# Revit family: BE_99408_de_DE
name_source: partatom
category: Leuchten
revit_build: Autodesk Revit 2015 (Build: 20160512_0715(x64)
units: mm (PartAtom-declared; Revit-internal decimal feet)

## types (4) — shared parameters
AC/DC = AC/DC
Aktualisierung = 2016-10-11T04:14:01
Anschlussleitung = 6.0 m X05BQ-F 4 × 1²
BEGA_Dummy = Nein
BEGA_IES = Ja
BEGA_Intern = Ja
BEGA_Intern_Konstruktion = Ja
BEGA_Intern_an = Ja
BEGA_Intern_aus = Ja
Beschreibung = Aufsatzleuchte
Beschreibung_Sonderanfertigung = Hier können Sie Informationen zur Sonderanfertigung eintragen.
CE_Konformität = ja
ENEC = ja
Einstecktiefe = 90 mm
Energieeffizienzklasse = LED A++ - A
Farbwiedergabeindex = Ra > 80
Frequenz = 0/50-60 Hz
Gewicht = 14.9 kg
Hersteller = BEGA
Lampe = LED 32 W
Lastklassifizierung = Beleuchtung
Lebensdauerkriterien = L70 = 50.000 h
Logo = BEGA_Logo.png
M_W = Nein
Material_02 = BEGA_Oberfläche_Silber_matt
Material_03 = BEGA_Oberfläche_Weiss_matt
Material_06 = BEGA_Oberfläche_Edelstahl_gebürstet
Material_09 = BEGA_Glas_klar
Material_10 = BEGA_Glas_matt
Material_11 = BEGA_Glas_opal
Material_15 = BEGA_Leuchtmedium_matt
Material_17 = BEGA_Reflektor
Produktdatenblatt = http://www.bega.de
Scheinlast = 0 VA
Schutzart = IP 65
Schutzklasse = II
Sonderanfertigung = Nein
Spannung = 240 V
Typenbild = 99408.png
URL = http://www.bega.de
Windangriffsfläche = 0.07 m²
zero-valued in all types: Vorgabe-Ansicht

## per-type parameters (varying)
| type | BEGA_IES1 | BEGA_IES2 | Bestellnummer | Farbtemperatur | LED_Modulbezeichnung | Lampenlichtstrom | Leuchtenlichtstrom | M_A | M_G | Modell |
| BEGA_99408_Grafit_K4 | Nein | Ja | 99408 | 4000 K | 2x LED-0469/840 + 2x LED-0472/840 | 8800 lm | 11628 lm | Nein | Ja | 99408 |
| BEGA_99408_Silber_K4 | Nein | Ja | 99408A | 4000 K | 2x LED-0469/840 + 2x LED-0472/840 | 8800 lm | 5814 lm | Ja | Nein | 99408A |
| BEGA_99408_Silber_K3 | Ja | Nein | 99408AK3 | 3000 K | 2x LED-0469/830 + 2x LED-0472/830 | 8280 lm | 5470 lm | Ja | Nein | 99408AK3 |
| BEGA_99408_Grafit_K3 | Ja | Nein | 99408K3 | 3000 K | 2x LED-0469/830 + 2x LED-0472/830 | 8280 lm | 5470 lm | Nein | Ja | 99408K3 |

## geometry (parser evidence)
native form markers: Sweep x4
no freeform markers — native parametric forms only
